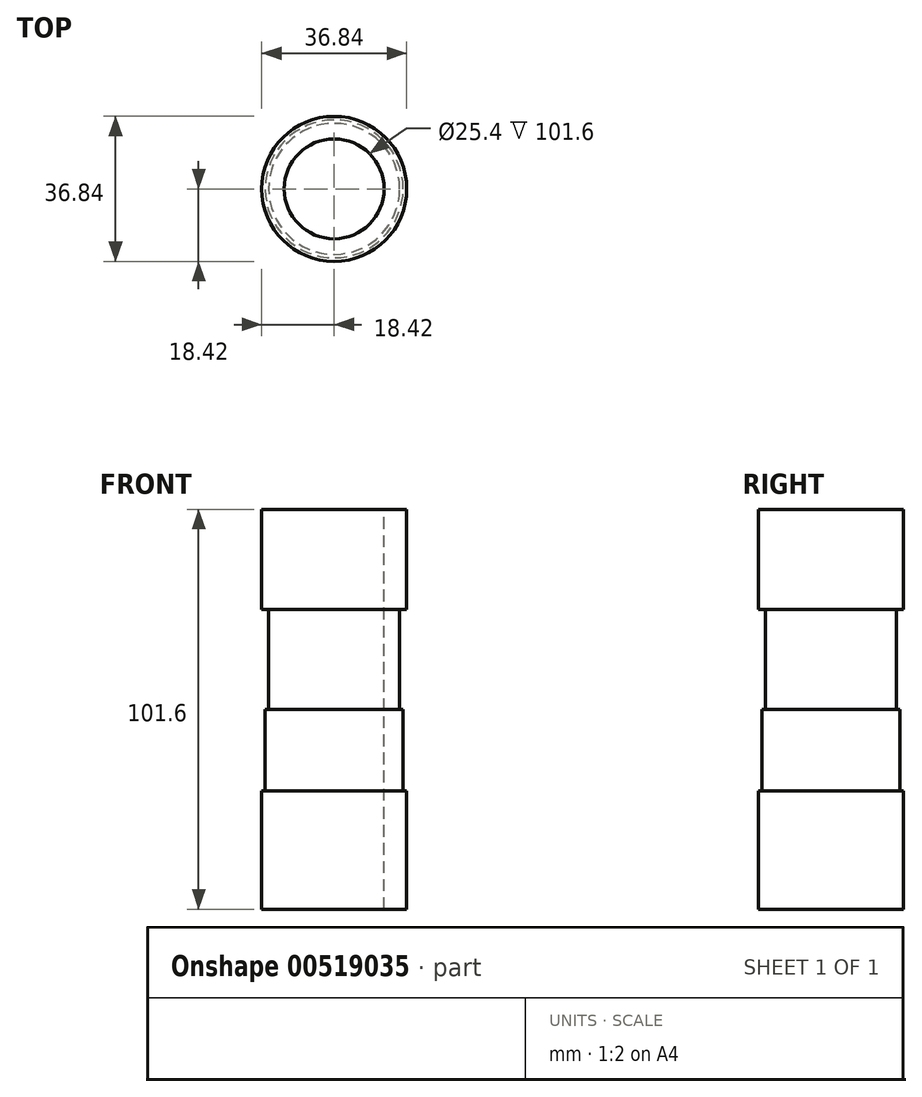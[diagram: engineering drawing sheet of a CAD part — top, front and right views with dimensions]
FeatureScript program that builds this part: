
annotation { "Feature Type Name" : "Feature", "Feature Type Description" : "" }
export const myFeature = defineFeature(function(context is Context, id is Id, definition is map)
    precondition{}
    {
        {
            var Q0;
            Q0=qCreatedBy(makeId("Front.planeOp"),FACE);
            var sketch = newSketch(context, id + "F0", { "sketchPlane" : qUnion([Q0])});
            skLineSegment(sketch, "E0", {"start": v(0, 76.67) * mm, "end": v(0, -76.24) * mm});
            skSolve(sketch);
        }
        {
            var Q0;
            Q0=qCreatedBy(makeId("Front.planeOp"),FACE);
            var sketch = newSketch(context, id + "F1", { "sketchPlane" : qUnion([Q0])});
            skLineSegment(sketch, "E1.bottom", {"start": v(12.7, 49.7) * mm, "end": v(18.41, 49.7) * mm});
            skLineSegment(sketch, "E1.top", {"start": v(12.7, -51.9) * mm, "end": v(18.41, -51.9) * mm});
            skLineSegment(sketch, "E1.left", {"start": v(12.7, 49.7) * mm, "end": v(12.7, -51.9) * mm});
            skLineSegment(sketch, "E1.right", {"start": v(18.41, 49.7) * mm, "end": v(18.41, 24.3) * mm});
            skLineSegment(sketch, "E2", {"start": v(18.41, 24.3) * mm, "end": v(16.64, 24.3) * mm});
            skLineSegment(sketch, "E3", {"start": v(16.64, 24.3) * mm, "end": v(16.64, -1.1) * mm});
            skLineSegment(sketch, "E4", {"start": v(16.64, -1.1) * mm, "end": v(17.53, -1.1) * mm});
            skLineSegment(sketch, "E5.trimOffspring", {"start": v(18.41, -21.9) * mm, "end": v(18.41, -51.9) * mm});
            skLineSegment(sketch, "E6", {"start": v(17.53, -1.1) * mm, "end": v(17.53, -21.9) * mm});
            skLineSegment(sketch, "E7", {"start": v(17.53, -21.9) * mm, "end": v(18.41, -21.9) * mm});
            skSolve(sketch);
        }
        {
            var Q0;
            Q0=makeQuery(id+"F1.imprint","IMPRINT",FACE,{"disambiguationData":[TD([[makeQuery(id+"F1.imprint","IMPRINT",EDGE,{"derivedFrom":sQuery(id+"F1.wireOp",EDGE,"E1.bottom")}),-1.0]])]});
            var Q1;
            Q1=sQuery(id+"F0.wireOp",EDGE,"E0");
            revolve(context, id + "F2", {"entities" : qUnion([Q0]), "axis" : qUnion([Q1]), "revolveType" : RevolveType.FULL});
        }
    });
